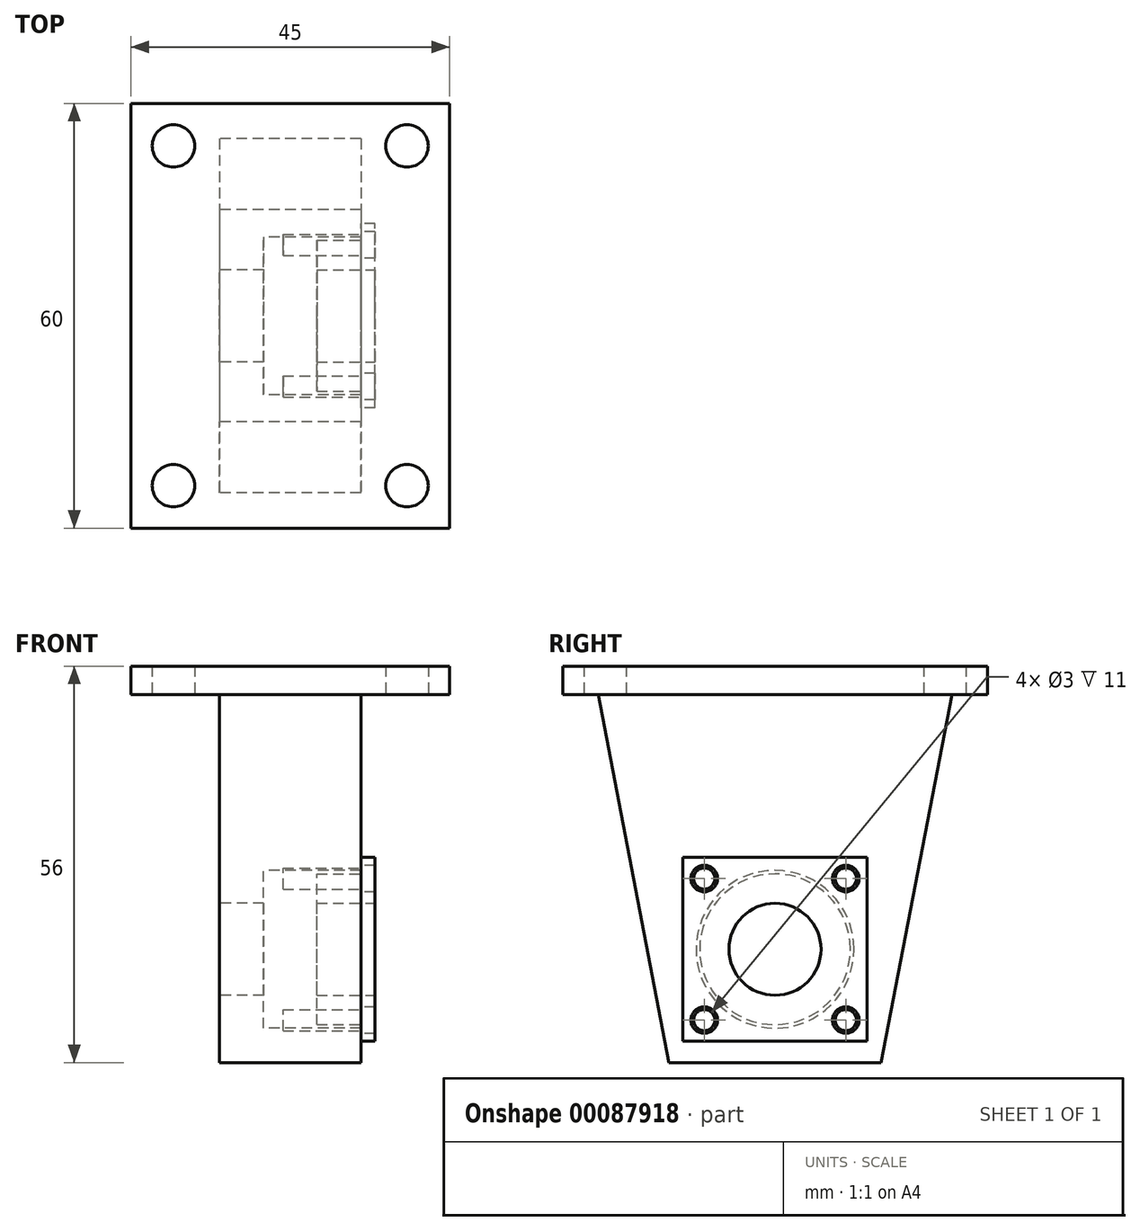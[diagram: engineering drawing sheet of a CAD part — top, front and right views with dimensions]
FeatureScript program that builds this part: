
annotation { "Feature Type Name" : "Feature", "Feature Type Description" : "" }
export const myFeature = defineFeature(function(context is Context, id is Id, definition is map)
    precondition{}
    {
        {
            var Q0;
            Q0=qCreatedBy(makeId("Top.planeOp"),FACE);
            var sketch = newSketch(context, id + "F0", { "sketchPlane" : qUnion([Q0])});
            skLineSegment(sketch, "E0.bottom", {"start": v(22.5, 30) * mm, "end": v(-22.5, 30) * mm});
            skLineSegment(sketch, "E0.top", {"start": v(22.5, -30) * mm, "end": v(-22.5, -30) * mm});
            skLineSegment(sketch, "E0.left", {"start": v(22.5, 30) * mm, "end": v(22.5, -30) * mm});
            skLineSegment(sketch, "E0.right", {"start": v(-22.5, 30) * mm, "end": v(-22.5, -30) * mm});
            skPoint(sketch, "E0.middle", {"position": v(0, 0) * mm});
            skCircle(sketch, "E1", {"center": v(-16.5, 24) * mm, "radius": 3 * mm});
            skCircle(sketch, "E2", {"center": v(-16.5, -24) * mm, "radius": 3 * mm});
            skCircle(sketch, "E3", {"center": v(16.5, 24) * mm, "radius": 3 * mm});
            skCircle(sketch, "E4", {"center": v(16.5, -24) * mm, "radius": 3 * mm});
            skSolve(sketch);
        }
        {
            var Q0;
            Q0=makeQuery(id+"F0.imprint","IMPRINT",FACE,{"disambiguationData":[TD([[makeQuery(id+"F0.imprint","IMPRINT",EDGE,{"derivedFrom":sQuery(id+"F0.wireOp",EDGE,"E0.bottom")}),1.0]])]});
            extrude(context, id + "F1", {"entities" : qUnion([Q0]), "depth" : 4 * mm});
        }
        {
            var Q0;
            Q0=qCreatedBy(makeId("Right.planeOp"),FACE);
            var sketch = newSketch(context, id + "F2", { "sketchPlane" : qUnion([Q0])});
            skLineSegment(sketch, "E5.bottom", {"start": v(25, 0) * mm, "end": v(-25, 0) * mm});
            skLineSegment(sketch, "E5.top", {"start": v(25, -52) * mm, "end": v(-25, -52) * mm});
            skLineSegment(sketch, "E5.left", {"start": v(25, 0) * mm, "end": v(25, -52) * mm});
            skLineSegment(sketch, "E5.right", {"start": v(-25, 0) * mm, "end": v(-25, -52) * mm});
            skLineSegment(sketch, "E6", {"start": v(25, 0) * mm, "end": v(15, -52) * mm});
            skLineSegment(sketch, "E7", {"start": v(-25, 0) * mm, "end": v(-15, -52) * mm});
            skCircle(sketch, "E8", {"center": v(0, -36) * mm, "radius": 11.15 * mm});
            skSolve(sketch);
        }
        {
            var Q0;
            Q0=makeQuery(id+"F2.imprint","IMPRINT",FACE,{"disambiguationData":[TD([[makeQuery(id+"F2.imprint","IMPRINT",EDGE,{"derivedFrom":sQuery(id+"F2.wireOp",EDGE,"E5.bottom")}),1.0]])]});
            extrude(context, id + "F3", {"entities" : qUnion([Q0]), "operationType" : NewBodyOperationType.ADD, "endBound" : BoundingType.SYMMETRIC, "depth" : 20 * mm});
        }
        {
            var Q0;
            Q0=makeQuery(id+"F3.opExtrude","CAP_FACE",FACE,{"disambiguationData":[OSD([sQuery(id+"F2.wireOp",EDGE,"E5.bottom"),sQuery(id+"F2.wireOp",EDGE,"E5.top"),sQuery(id+"F2.wireOp",EDGE,"E6"),sQuery(id+"F2.wireOp",EDGE,"E7"),sQuery(id+"F2.wireOp",EDGE,"E8")])],"isStart":true});
            var sketch = newSketch(context, id + "F4", { "sketchPlane" : qUnion([Q0])});
            skCircle(sketch, "E9", {"center": v(0, -36) * mm, "radius": 11.15 * mm});
            skCircle(sketch, "E10", {"center": v(0, -36) * mm, "radius": 6.5 * mm});
            skSolve(sketch);
        }
        {
            var Q0;
            Q0=makeQuery(id+"F4.imprint","IMPRINT",FACE,{"disambiguationData":[TD([[makeQuery(id+"F4.imprint","IMPRINT",EDGE,{"derivedFrom":sQuery(id+"F4.wireOp",EDGE,"E9")}),-1.0]])]});
            extrude(context, id + "F5", {"entities" : qUnion([Q0]), "operationType" : NewBodyOperationType.ADD, "oppositeDirection" : true, "depth" : 6.25 * mm});
        }
        {
            var Q0;
            Q0=makeQuery(id+"F3.opExtrude","CAP_FACE",FACE,{"disambiguationData":[OSD([sQuery(id+"F2.wireOp",EDGE,"E5.bottom"),sQuery(id+"F2.wireOp",EDGE,"E5.top"),sQuery(id+"F2.wireOp",EDGE,"E6"),sQuery(id+"F2.wireOp",EDGE,"E7"),sQuery(id+"F2.wireOp",EDGE,"E8")])],"isStart":false});
            var sketch = newSketch(context, id + "F6", { "sketchPlane" : qUnion([Q0])});
            skCircle(sketch, "E11", {"center": v(0, -36) * mm, "radius": 10.65 * mm});
            skCircle(sketch, "E12", {"center": v(0, -36) * mm, "radius": 6.5 * mm});
            skLineSegment(sketch, "E13.bottom", {"start": v(-13, -23) * mm, "end": v(13, -23) * mm});
            skLineSegment(sketch, "E13.top", {"start": v(-13, -49) * mm, "end": v(13, -49) * mm});
            skLineSegment(sketch, "E13.left", {"start": v(-13, -23) * mm, "end": v(-13, -49) * mm});
            skLineSegment(sketch, "E13.right", {"start": v(13, -23) * mm, "end": v(13, -49) * mm});
            skCircle(sketch, "E14", {"center": v(-10, -26) * mm, "radius": 1.88 * mm});
            skCircle(sketch, "E15", {"center": v(10, -26) * mm, "radius": 1.88 * mm});
            skCircle(sketch, "E16", {"center": v(-10, -46) * mm, "radius": 1.88 * mm});
            skCircle(sketch, "E17", {"center": v(10, -46) * mm, "radius": 1.88 * mm});
            skSolve(sketch);
        }
        {
            var Q0;
            Q0=makeQuery(id+"F6.imprint","IMPRINT",FACE,{"disambiguationData":[TD([[makeQuery(id+"F6.imprint","IMPRINT",EDGE,{"derivedFrom":sQuery(id+"F6.wireOp",EDGE,"E11")}),1.0]])]});
            extrude(context, id + "F7", {"entities" : qUnion([Q0]), "oppositeDirection" : true, "depth" : 6.25 * mm});
        }
        {
            var Q0;
            Q0=makeQuery(id+"F6.imprint","IMPRINT",FACE,{"disambiguationData":[TD([[makeQuery(id+"F6.imprint","IMPRINT",EDGE,{"derivedFrom":sQuery(id+"F6.wireOp",EDGE,"E13.bottom")}),-1.0]])]});
            var Q1;
            Q1=makeQuery(id+"F6.imprint","IMPRINT",FACE,{"disambiguationData":[TD([[makeQuery(id+"F6.imprint","IMPRINT",EDGE,{"derivedFrom":sQuery(id+"F6.wireOp",EDGE,"E11")}),-1.0]])]});
            var Q2;
            Q2=makeQuery(id+"F6.imprint","IMPRINT",FACE,{"disambiguationData":[TD([[makeQuery(id+"F6.imprint","IMPRINT",EDGE,{"derivedFrom":sQuery(id+"F6.wireOp",EDGE,"E11")}),1.0]])]});
            extrude(context, id + "F8", {"entities" : qUnion([Q0, Q1, Q2]), "operationType" : NewBodyOperationType.ADD, "depth" : 2 * mm});
        }
        {
            var Q0;
            Q0=makeQuery(id+"F6.imprint","IMPRINT",FACE,{"disambiguationData":[TD([[makeQuery(id+"F6.imprint","IMPRINT",EDGE,{"derivedFrom":sQuery(id+"F6.wireOp",EDGE,"E13.bottom")}),1.0]])]});
            var sketch = newSketch(context, id + "F9", { "sketchPlane" : qUnion([Q0])});
            skCircle(sketch, "E18", {"center": v(-10, -26) * mm, "radius": 1.5 * mm});
            skCircle(sketch, "E19", {"center": v(10, -26) * mm, "radius": 1.5 * mm});
            skCircle(sketch, "E20", {"center": v(10, -46) * mm, "radius": 1.5 * mm});
            skCircle(sketch, "E21", {"center": v(-10, -46) * mm, "radius": 1.5 * mm});
            skSolve(sketch);
        }
        {
            var Q0;
            Q0=makeQuery(id+"F9.imprint","IMPRINT",FACE,{"disambiguationData":[TD([[makeQuery(id+"F9.imprint","IMPRINT",EDGE,{"derivedFrom":sQuery(id+"F9.wireOp",EDGE,"E18")}),1.0]])]});
            var Q1;
            Q1=makeQuery(id+"F9.imprint","IMPRINT",FACE,{"disambiguationData":[TD([[makeQuery(id+"F9.imprint","IMPRINT",EDGE,{"derivedFrom":sQuery(id+"F9.wireOp",EDGE,"E19")}),1.0]])]});
            var Q2;
            Q2=makeQuery(id+"F9.imprint","IMPRINT",FACE,{"disambiguationData":[TD([[makeQuery(id+"F9.imprint","IMPRINT",EDGE,{"derivedFrom":sQuery(id+"F9.wireOp",EDGE,"E20")}),1.0]])]});
            var Q3;
            Q3=makeQuery(id+"F9.imprint","IMPRINT",FACE,{"disambiguationData":[TD([[makeQuery(id+"F9.imprint","IMPRINT",EDGE,{"derivedFrom":sQuery(id+"F9.wireOp",EDGE,"E21")}),1.0]])]});
            extrude(context, id + "F10", {"entities" : qUnion([Q0, Q1, Q2, Q3]), "operationType" : NewBodyOperationType.REMOVE, "oppositeDirection" : true, "depth" : 11 * mm});
        }
    });
